# Revit family: QF_ELECTROLUXPROFESSIONAL_1LSNLJ_IC64821FLF_G
name_source: partatom
category: Attrezzature speciali
units: mm (PartAtom-declared; Revit-internal decimal feet)

## family parameters
Basato su piano di lavoro = No
Condiviso = No
Punto di calcolo locali = No
Quota connettore circolare = Usa diametro
Sempre verticale = Sì
Taglio con vuoti quando caricato = No
Tipo di parte = Normale

## types (5) — shared parameters
Depth Actual = 1320 mm
Gas KW = 44
Height Actual = 1460 mm  [stored 4.79003 ft]
Latent Heat Output = 0.0
Length Actual = 2775 mm  [stored 9.10433 ft]
Modello = IC64821FLF
Phase = 3
Produttore = Electrolux Professional
Sensible Heat Output = 0.0
URL = www.electroluxprofessional.com
Weight = 1100
zero-valued in all types: Prospetto di default, Steam Pounds per Hour

## per-type parameters (varying)
| type | Cycle | Descrizione | Item Number | Volts | Watts |
| 9882030313 | 60 Hz | IRONER CYLINDER IC64821FLF FEEDING+LENGTH FOLDING 2120MM SUPERIOR GAS CE 208-240/60/3 DUBIXIUM EN-ES-PO VAC.FEED.TABLE A | 1L82DH | 240 V | 1400 W |
| 9882030236 | 50 Hz | IRONER CYLINDER IC64821FLF FEEDING+LENGTH FOLDING 2120MM SUPERIOR GAS CE 400/50/3 DUBIXIUM FR VAC.FEED.TABLE ANTISTATIC | 1L0GW1 | 400 V | 1750 W |
| 9882030314 | 50 Hz | IRONER CYLINDER IC64821FLF FEEDING+LENGTH FOLDING 2120MM SUPERIOR GAS CE 400/50/3 DUBIXIUM ML VAC.FEED.TABLE ANTISTATIC | 1LT6BS | 400 V | 1750 W |
| 9882030310 | 50 Hz | IRONER CYLINDER IC64821FLF FEEDING+LENGTH FOLDING 2120MM GAS CE 400/50/3 6MM SST CYL. ML VAC.FEED.TABLE ANTISTATIC DIAMM | 1L0HEF | 400 V | 1750 W |
| 9882030255 | 60 Hz | IRONER CYLINDER IC64821FLF FEEDING+LENGTH FOLDING 2120MM SUPERIOR GAS CE 400/60/3 DUBIXIUM ML VAC.FEED.TABLE ANTISTATIC | 1L0GZK | 400 V | 1750 W |

note: [stored X ft] marks values corroborated as IEEE doubles in the binary element streams (Revit-internal decimal feet)

## geometry (parser evidence)
native form markers: Sweep x10
no freeform markers — native parametric forms only
